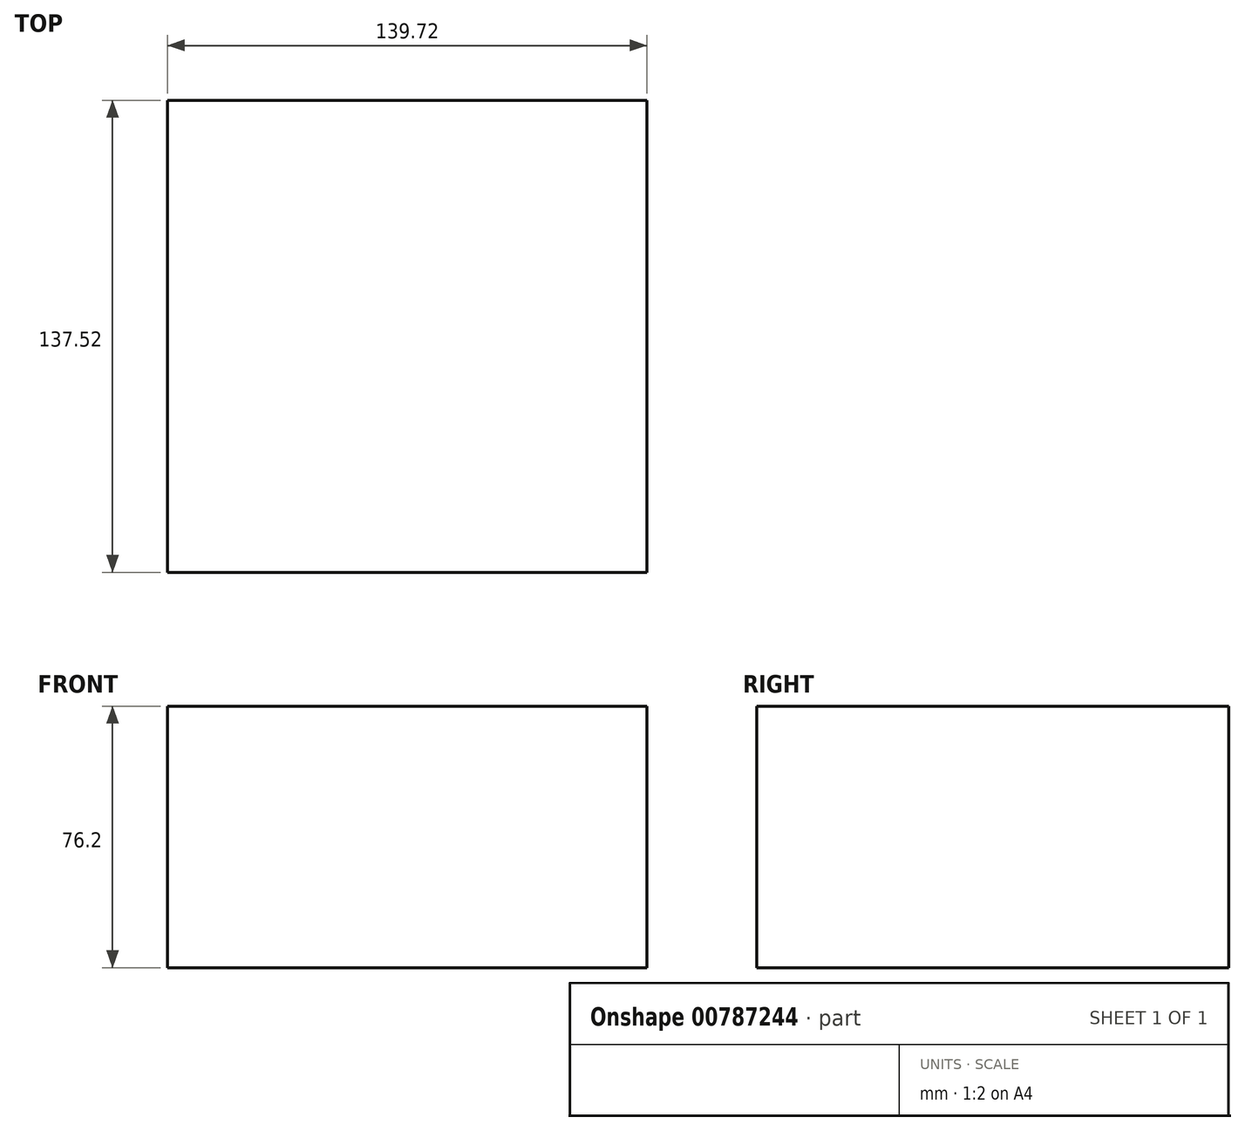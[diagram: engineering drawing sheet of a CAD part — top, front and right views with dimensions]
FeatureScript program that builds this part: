
annotation { "Feature Type Name" : "Feature", "Feature Type Description" : "" }
export const myFeature = defineFeature(function(context is Context, id is Id, definition is map)
    precondition{}
    {
        {
            var Q0;
            Q0=qCreatedBy(makeId("Top.planeOp"),FACE);
            var sketch = newSketch(context, id + "F0", { "sketchPlane" : qUnion([Q0])});
            skLineSegment(sketch, "E0.bottom", {"start": v(69.86, -68.76) * mm, "end": v(-69.86, -68.76) * mm});
            skLineSegment(sketch, "E0.top", {"start": v(69.86, 68.76) * mm, "end": v(-69.86, 68.76) * mm});
            skLineSegment(sketch, "E0.left", {"start": v(69.86, -68.76) * mm, "end": v(69.86, 68.76) * mm});
            skLineSegment(sketch, "E0.right", {"start": v(-69.86, -68.76) * mm, "end": v(-69.86, 68.76) * mm});
            skPoint(sketch, "E0.middle", {"position": v(0, 0) * mm});
            skLineSegment(sketch, "E1", {"start": v(0, 68.76) * mm, "end": v(0, -68.76) * mm});
            skSolve(sketch);
        }
        {
            var Q0;
            Q0=qCreatedBy(makeId("Top.planeOp"),FACE);
            var sketch = newSketch(context, id + "F1", { "sketchPlane" : qUnion([Q0])});
            skCircle(sketch, "E2", {"center": v(54.26, 0) * mm, "radius": 9.82 * mm});
            skSolve(sketch);
        }
        {
            var Q0;
            {var subQ0=sQuery(id+"F0.wireOp",EDGE,"E0.right");Q0=makeQuery(id+"F0.imprint","IMPRINT",FACE,{"disambiguationData":[TD([[makeQuery(id+"F0.imprint","IMPRINT",EDGE,{"derivedFrom":subQ0}),-1.0]])]});}
            extrude(context, id + "F2", {"entities" : qUnion([Q0]), "depth" : -76.2 * mm, "offsetDistance" : 25.4 * mm});
        }
        {
            var Q0;
            {var subQ0=sQuery(id+"F0.wireOp",EDGE,"E0.left");Q0=makeQuery(id+"F0.imprint","IMPRINT",FACE,{"disambiguationData":[TD([[makeQuery(id+"F0.imprint","IMPRINT",EDGE,{"derivedFrom":subQ0}),1.0]])]});}
            extrude(context, id + "F3", {"entities" : qUnion([Q0]), "operationType" : NewBodyOperationType.ADD, "depth" : -76.2 * mm, "offsetDistance" : 25.4 * mm});
        }
        {
            var Q0;
            Q0=sQuery(id+"F1.wireOp",EDGE,"E2");
            var Q1;
            Q1=sQuery(id+"F0.wireOp",EDGE,"E1");
            revolve(context, id + "F4", {"bodyType" : ToolBodyType.SURFACE, "surfaceOperationType" : NewSurfaceOperationType.NEW, "surfaceEntities" : qUnion([Q0]), "axis" : qUnion([Q1]), "revolveType" : RevolveType.FULL});
        }
    });
